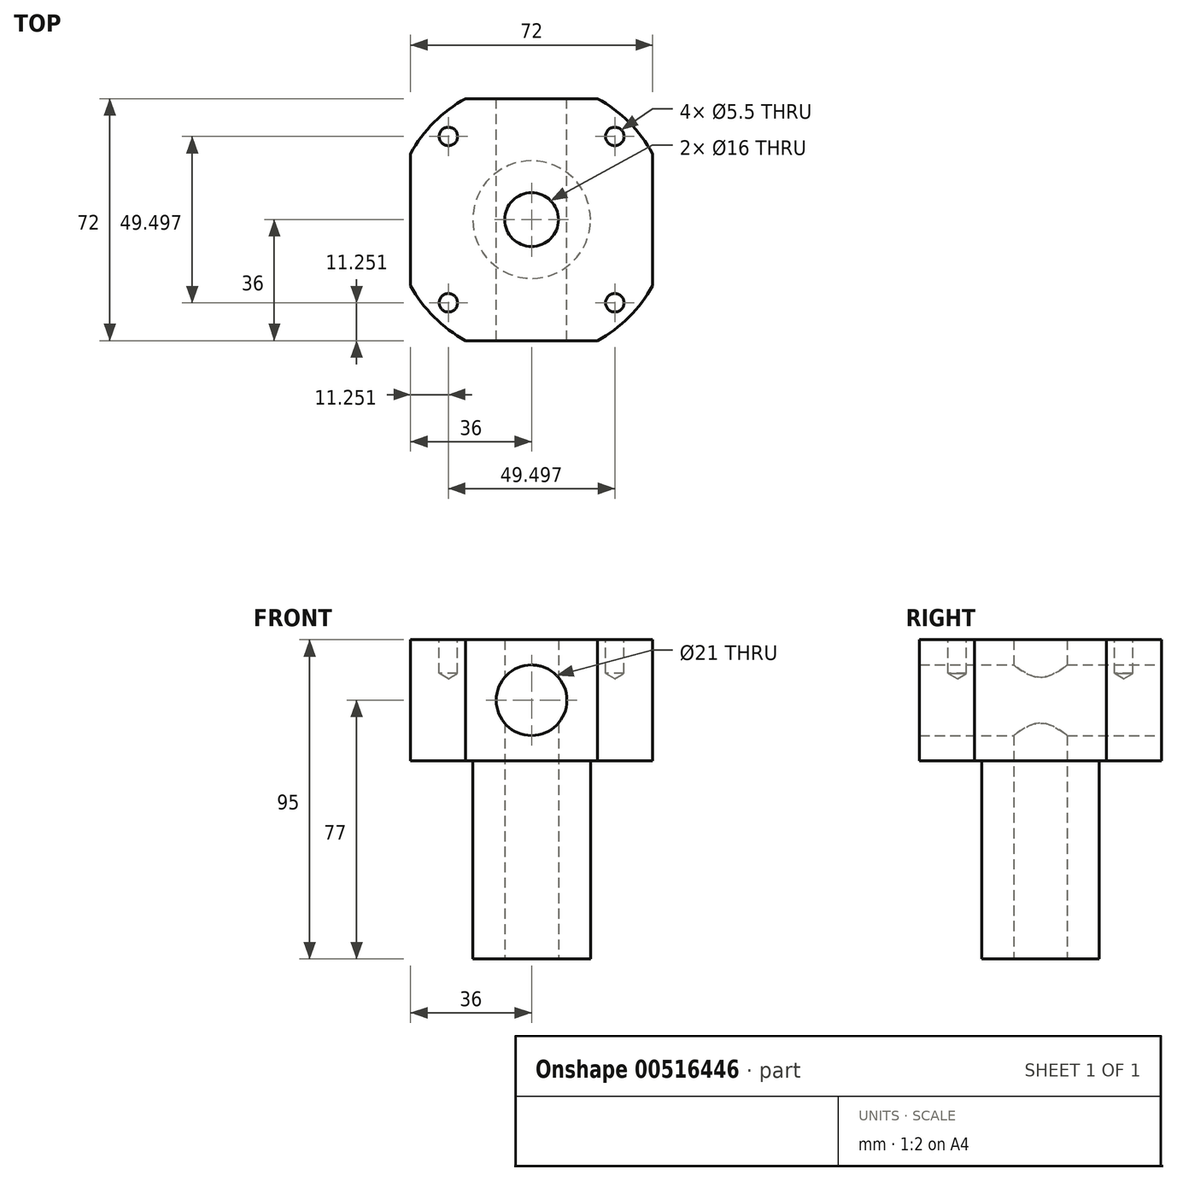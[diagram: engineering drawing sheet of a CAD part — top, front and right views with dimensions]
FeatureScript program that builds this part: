
annotation { "Feature Type Name" : "Feature", "Feature Type Description" : "" }
export const myFeature = defineFeature(function(context is Context, id is Id, definition is map)
    precondition{}
    {
        {
            var Q0;
            Q0=qCreatedBy(makeId("Top.planeOp"),FACE);
            var sketch = newSketch(context, id + "F0", { "sketchPlane" : qUnion([Q0])});
            skArc(sketch, "E0", {"start": v(-19.62, 36) * mm, "mid": v(-29, 29) * mm, "end": v(-36, 19.62) * mm});
            skLineSegment(sketch, "E1.bottom", {"start": v(-19.62, 36) * mm, "end": v(19.62, 36) * mm});
            skLineSegment(sketch, "E1.top", {"start": v(-19.62, -36) * mm, "end": v(19.62, -36) * mm});
            skLineSegment(sketch, "E1.left", {"start": v(-36, 19.62) * mm, "end": v(-36, -19.62) * mm});
            skLineSegment(sketch, "E1.right", {"start": v(36, 19.62) * mm, "end": v(36, -19.62) * mm});
            skArc(sketch, "E2.trimOffspring", {"start": v(36, 19.62) * mm, "mid": v(29, 29) * mm, "end": v(19.62, 36) * mm});
            skArc(sketch, "E3.trimOffspring", {"start": v(19.62, -36) * mm, "mid": v(29, -29) * mm, "end": v(36, -19.62) * mm});
            skArc(sketch, "E4.trimOffspring", {"start": v(-36, -19.62) * mm, "mid": v(-29, -29) * mm, "end": v(-19.62, -36) * mm});
            skSolve(sketch);
        }
        {
            var Q0;
            Q0 = qSketchRegion(id + "F0", true);
            extrude(context, id + "F1", {"entities" : qUnion([Q0]), "depth" : 36 * mm, "offsetDistance" : 25 * mm});
        }
        {
            var Q0;
            Q0=makeQuery(id+"F1.opExtrude","CAP_FACE",FACE,{"disambiguationData":[OSD([sQuery(id+"F0.wireOp",EDGE,"E0"),sQuery(id+"F0.wireOp",EDGE,"E1.bottom"),sQuery(id+"F0.wireOp",EDGE,"E1.top"),sQuery(id+"F0.wireOp",EDGE,"E1.left"),sQuery(id+"F0.wireOp",EDGE,"E1.right"),sQuery(id+"F0.wireOp",EDGE,"E2.trimOffspring"),sQuery(id+"F0.wireOp",EDGE,"E3.trimOffspring"),sQuery(id+"F0.wireOp",EDGE,"E4.trimOffspring")])],"isStart":false});
            var sketch = newSketch(context, id + "F2", { "sketchPlane" : qUnion([Q0])});
            skCircle(sketch, "E5", {"center": v(0, 0) * mm, "radius": 35 * mm, "construction": true});
            skLineSegment(sketch, "E6", {"start": v(0, 0) * mm, "end": v(24.75, 24.75) * mm, "construction": true});
            skLineSegment(sketch, "E7", {"start": v(0, 0) * mm, "end": v(-24.75, 24.75) * mm, "construction": true});
            skPoint(sketch, "E8", {"position": v(-24.75, 24.75) * mm});
            skPoint(sketch, "E9", {"position": v(24.75, 24.75) * mm});
            skPoint(sketch, "E10", {"position": v(24.75, -24.75) * mm});
            skPoint(sketch, "E11", {"position": v(-24.75, -24.75) * mm});
            skSolve(sketch);
        }
        {
            var Q0;
            Q0=sQuery(id+"F2.wireOp",VERTEX,"E8");
            var Q1;
            Q1=sQuery(id+"F2.wireOp",VERTEX,"E9");
            var Q2;
            Q2=sQuery(id+"F2.wireOp",VERTEX,"E10");
            var Q3;
            Q3=sQuery(id+"F2.wireOp",VERTEX,"E11");
            var Q4;
            Q4=makeQuery(id+"F1.opExtrude","SWEPT_BODY",BODY,{"disambiguationData":[OSD([sQuery(id+"F0.wireOp",EDGE,"E0"),sQuery(id+"F0.wireOp",EDGE,"E1.bottom"),sQuery(id+"F0.wireOp",EDGE,"E1.top"),sQuery(id+"F0.wireOp",EDGE,"E1.left"),sQuery(id+"F0.wireOp",EDGE,"E1.right"),sQuery(id+"F0.wireOp",EDGE,"E2.trimOffspring"),sQuery(id+"F0.wireOp",EDGE,"E3.trimOffspring"),sQuery(id+"F0.wireOp",EDGE,"E4.trimOffspring")])]});
            hole(context, id + "F3", {"style" : HoleStyle.SIMPLE, "endStyle" : HoleEndStyle.BLIND, "standardTappedOrClearance" : lookupTablePath({ "standard" : "ISO", "fit" : "Normal", "size" : "M5", "type" : "Clearance" }), "standardBlindInLast" : lookupTablePath({ "fit" : "Standard", "standard" : "ISO", "size" : "M5", "type" : "Clearance" }), "holeDiameter" : 5.5 * mm, "majorDiameter" : 5 * mm, "holeDepth" : 10 * mm, "isTappedThrough" : true, "tappedDepth" : 12 * mm, "tapClearance" : 3, "startFromSketch" : true, "locations" : qUnion([Q0, Q1, Q2, Q3]), "scope" : qUnion([Q4])});
        }
        {
            var Q0;
            Q0=makeQuery(id+"F1.opExtrude","CAP_FACE",FACE,{"disambiguationData":[OSD([sQuery(id+"F0.wireOp",EDGE,"E0"),sQuery(id+"F0.wireOp",EDGE,"E1.bottom"),sQuery(id+"F0.wireOp",EDGE,"E1.top"),sQuery(id+"F0.wireOp",EDGE,"E1.left"),sQuery(id+"F0.wireOp",EDGE,"E1.right"),sQuery(id+"F0.wireOp",EDGE,"E2.trimOffspring"),sQuery(id+"F0.wireOp",EDGE,"E3.trimOffspring"),sQuery(id+"F0.wireOp",EDGE,"E4.trimOffspring")])],"isStart":false});
            var sketch = newSketch(context, id + "F4", { "sketchPlane" : qUnion([Q0])});
            skCircle(sketch, "E12", {"center": v(0, 0) * mm, "radius": 8 * mm});
            skSolve(sketch);
        }
        {
            var Q0;
            Q0=makeQuery(id+"F1.opExtrude","CAP_FACE",FACE,{"disambiguationData":[OSD([sQuery(id+"F0.wireOp",EDGE,"E0"),sQuery(id+"F0.wireOp",EDGE,"E1.bottom"),sQuery(id+"F0.wireOp",EDGE,"E1.top"),sQuery(id+"F0.wireOp",EDGE,"E1.left"),sQuery(id+"F0.wireOp",EDGE,"E1.right"),sQuery(id+"F0.wireOp",EDGE,"E2.trimOffspring"),sQuery(id+"F0.wireOp",EDGE,"E3.trimOffspring"),sQuery(id+"F0.wireOp",EDGE,"E4.trimOffspring")])],"isStart":true});
            var sketch = newSketch(context, id + "F5", { "sketchPlane" : qUnion([Q0])});
            skCircle(sketch, "E13", {"center": v(0, 0) * mm, "radius": 17.5 * mm});
            skSolve(sketch);
        }
        {
            var Q0;
            Q0 = qSketchRegion(id + "F5", true);
            extrude(context, id + "F6", {"entities" : qUnion([Q0]), "operationType" : NewBodyOperationType.ADD, "depth" : 59 * mm, "offsetDistance" : 25 * mm});
        }
        {
            var Q0;
            Q0=makeQuery(id+"F6.opExtrude","CAP_FACE",FACE,{"disambiguationData":[OSD([sQuery(id+"F5.wireOp",EDGE,"E13")])],"isStart":false});
            var sketch = newSketch(context, id + "F7", { "sketchPlane" : qUnion([Q0])});
            skCircle(sketch, "E14", {"center": v(0, 0) * mm, "radius": 8 * mm});
            skSolve(sketch);
        }
        {
            var Q0;
            Q0=makeQuery(id+"F7.imprint","IMPRINT",FACE,{"disambiguationData":[TD([[makeQuery(id+"F7.imprint","IMPRINT",EDGE,{"derivedFrom":sQuery(id+"F7.wireOp",EDGE,"E14")}),1.0]])]});
            var Q1;
            Q1=sQuery(id+"F7.wireOp",EDGE,"E14");
            extrude(context, id + "F8", {"entities" : qUnion([Q0]), "operationType" : NewBodyOperationType.REMOVE, "surfaceEntities" : qUnion([Q1]), "endBound" : BoundingType.THROUGH_ALL, "oppositeDirection" : true, "depth" : 25 * mm, "offsetDistance" : 25 * mm});
        }
        {
            var Q0;
            Q0=makeQuery(id+"F1.opExtrude","SWEPT_FACE",FACE,{"disambiguationData":[OSD([sQuery(id+"F0.wireOp",EDGE,"E1.bottom")])]});
            var sketch = newSketch(context, id + "F9", { "sketchPlane" : qUnion([Q0])});
            skPoint(sketch, "E15", {"position": v(0, 18) * mm});
            skSolve(sketch);
        }
        {
            var Q0;
            Q0=sQuery(id+"F9.wireOp",VERTEX,"E15");
            var Q1;
            Q1=makeQuery(id+"F1.opExtrude","SWEPT_BODY",BODY,{"disambiguationData":[OSD([sQuery(id+"F0.wireOp",EDGE,"E0"),sQuery(id+"F0.wireOp",EDGE,"E1.bottom"),sQuery(id+"F0.wireOp",EDGE,"E1.top"),sQuery(id+"F0.wireOp",EDGE,"E1.left"),sQuery(id+"F0.wireOp",EDGE,"E1.right"),sQuery(id+"F0.wireOp",EDGE,"E2.trimOffspring"),sQuery(id+"F0.wireOp",EDGE,"E3.trimOffspring"),sQuery(id+"F0.wireOp",EDGE,"E4.trimOffspring")])]});
            hole(context, id + "F10", {"style" : HoleStyle.SIMPLE, "endStyle" : HoleEndStyle.THROUGH, "standardTappedOrClearance" : lookupTablePath({ "standard" : "ISO", "fit" : "Close", "size" : "M20", "type" : "Clearance" }), "standardBlindInLast" : lookupTablePath({ "fit" : "Close", "standard" : "ISO", "size" : "M20", "type" : "Clearance" }), "holeDiameter" : 21 * mm, "majorDiameter" : 5 * mm, "isTappedThrough" : true, "tappedDepth" : 12 * mm, "tapClearance" : 3, "startFromSketch" : true, "locations" : qUnion([Q0]), "scope" : qUnion([Q1])});
        }
    });
